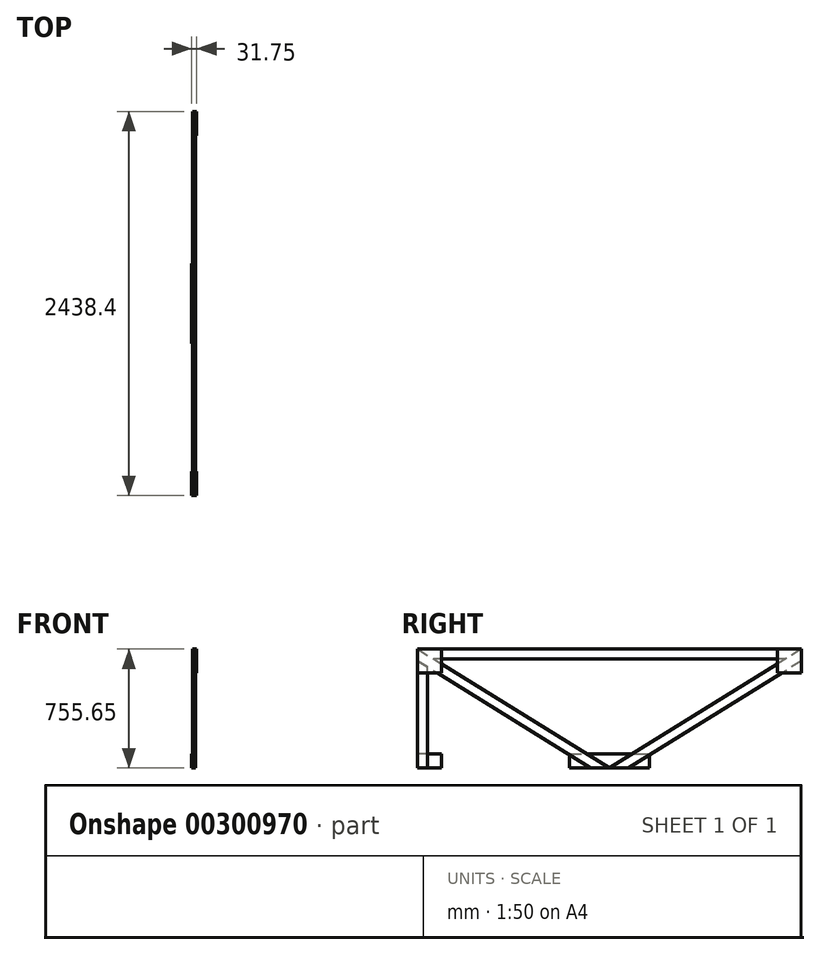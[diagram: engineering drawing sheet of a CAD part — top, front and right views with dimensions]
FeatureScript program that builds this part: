
annotation { "Feature Type Name" : "Feature", "Feature Type Description" : "" }
export const myFeature = defineFeature(function(context is Context, id is Id, definition is map)
    precondition{}
    {
        {
            var Q0;
            Q0=qCreatedBy(makeId("Right.planeOp"),FACE);
            var sketch = newSketch(context, id + "F0", { "sketchPlane" : qUnion([Q0])});
            skLineSegment(sketch, "E0.bottom", {"start": v(0, 0) * mm, "end": v(2438.4, 0) * mm, "construction": true});
            skLineSegment(sketch, "E0.left", {"start": v(0, 0) * mm, "end": v(0, 755.65) * mm, "construction": true});
            skLineSegment(sketch, "E0.right", {"start": v(2438.4, 0) * mm, "end": v(2438.4, 764.91) * mm, "construction": true});
            skLineSegment(sketch, "E1", {"start": v(0, 755.65) * mm, "end": v(1219.2, 0) * mm});
            skLineSegment(sketch, "E2.0", {"start": v(0, 680.94) * mm, "end": v(1098.66, 0) * mm});
            skLineSegment(sketch, "E3", {"start": v(0, 755.65) * mm, "end": v(0, 680.94) * mm});
            skLineSegment(sketch, "E4", {"start": v(1219.2, 0) * mm, "end": v(1098.66, 0) * mm});
            skLineSegment(sketch, "E5", {"start": v(1219.2, 0) * mm, "end": v(1219.2, 1098.2) * mm, "construction": true});
            skPoint(sketch, "E5.endSnap0", {"position": v(1219.2, 822.37) * mm});
            skLineSegment(sketch, "E6", {"start": v(1219.2, 755.65) * mm, "end": v(0, 755.65) * mm});
            skLineSegment(sketch, "E7.0", {"start": v(1221.99, 692.15) * mm, "end": v(102.45, 692.15) * mm});
            skLineSegment(sketch, "E8", {"start": v(0, 755.65) * mm, "end": v(102.45, 692.15) * mm});
            skLineSegment(sketch, "E9.MirrorCS", {"start": v(2438.4, 755.65) * mm, "end": v(2438.4, 680.94) * mm});
            skLineSegment(sketch, "E10.MirrorCS", {"start": v(2438.4, 680.94) * mm, "end": v(1339.74, 0) * mm});
            skLineSegment(sketch, "E11.MirrorCS", {"start": v(2438.4, 755.65) * mm, "end": v(1219.2, 0) * mm});
            skLineSegment(sketch, "E12.MirrorCS", {"start": v(2438.4, 755.65) * mm, "end": v(2335.95, 692.15) * mm});
            skLineSegment(sketch, "E13.MirrorCS", {"start": v(1219.2, 755.65) * mm, "end": v(2438.4, 755.65) * mm});
            skLineSegment(sketch, "E14.MirrorCS", {"start": v(1216.41, 692.15) * mm, "end": v(2335.95, 692.15) * mm});
            skLineSegment(sketch, "E15.MirrorCS", {"start": v(1219.2, 0) * mm, "end": v(1339.74, 0) * mm});
            skSolve(sketch);
        }
        {
            var Q0;
            {var subQ3=sQuery(id+"F0.wireOp",EDGE,"E9.MirrorCS");Q0=makeQuery(id+"F0.imprint","IMPRINT",FACE,{"disambiguationData":[TD([[makeQuery(id+"F0.imprint","IMPRINT",EDGE,{"derivedFrom":subQ3}),-1.0]])]});}
            var Q1;
            Q1=makeQuery(id+"F0.imprint","IMPRINT",FACE,{"disambiguationData":[TD([[makeQuery(id+"F0.imprint","IMPRINT",EDGE,{"derivedFrom":sQuery(id+"F0.wireOp",EDGE,"E2.0")}),1.0]])]});
            extrude(context, id + "F1", {"entities" : qUnion([Q0, Q1]), "depth" : 19.05 * mm});
        }
        {
            var Q0;
            Q0=makeQuery(id+"F0.imprint","IMPRINT",FACE,{"disambiguationData":[TD([[makeQuery(id+"F0.imprint","IMPRINT",EDGE,{"derivedFrom":sQuery(id+"F0.wireOp",EDGE,"E6")}),1.0]])]});
            extrude(context, id + "F2", {"entities" : qUnion([Q0]), "depth" : 19.05 * mm});
        }
        {
            var Q0;
            Q0=makeQuery(id+"F1.opExtrude","CAP_FACE",FACE,{"disambiguationData":[OSD([sQuery(id+"F0.wireOp",EDGE,"E9.MirrorCS"),sQuery(id+"F0.wireOp",EDGE,"E10.MirrorCS"),sQuery(id+"F0.wireOp",EDGE,"E11.MirrorCS"),sQuery(id+"F0.wireOp",EDGE,"E12.MirrorCS"),sQuery(id+"F0.wireOp",EDGE,"E15.MirrorCS")])],"isStart":false});
            var sketch = newSketch(context, id + "F3", { "sketchPlane" : qUnion([Q0])});
            skLineSegment(sketch, "E16.bottom", {"start": v(2438.4, 755.65) * mm, "end": v(2286, 755.65) * mm});
            skLineSegment(sketch, "E16.top", {"start": v(2438.4, 603.25) * mm, "end": v(2286, 603.25) * mm});
            skLineSegment(sketch, "E16.left", {"start": v(2438.4, 755.65) * mm, "end": v(2438.4, 603.25) * mm});
            skLineSegment(sketch, "E16.right", {"start": v(2286, 755.65) * mm, "end": v(2286, 603.25) * mm});
            skLineSegment(sketch, "E17", {"start": v(1219.2, 0) * mm, "end": v(1219.2, 1007.92) * mm, "construction": true});
            skLineSegment(sketch, "E18.MirrorCS", {"start": v(152.4, 755.65) * mm, "end": v(152.4, 603.25) * mm});
            skLineSegment(sketch, "E19.MirrorCS", {"start": v(0, 755.65) * mm, "end": v(0, 603.25) * mm});
            skLineSegment(sketch, "E20.MirrorCS", {"start": v(0, 603.25) * mm, "end": v(152.4, 603.25) * mm});
            skLineSegment(sketch, "E21.MirrorCS", {"start": v(0, 755.65) * mm, "end": v(152.4, 755.65) * mm});
            skSolve(sketch);
        }
        {
            var Q0;
            Q0 = qSketchRegion(id + "F3", true);
            extrude(context, id + "F4", {"entities" : qUnion([Q0]), "depth" : 6.35 * mm});
        }
        {
            var Q0;
            Q0=makeQuery(id+"F1.opExtrude","CAP_FACE",FACE,{"disambiguationData":[OSD([sQuery(id+"F0.wireOp",EDGE,"E9.MirrorCS"),sQuery(id+"F0.wireOp",EDGE,"E10.MirrorCS"),sQuery(id+"F0.wireOp",EDGE,"E11.MirrorCS"),sQuery(id+"F0.wireOp",EDGE,"E12.MirrorCS"),sQuery(id+"F0.wireOp",EDGE,"E15.MirrorCS")])],"isStart":true});
            var sketch = newSketch(context, id + "F5", { "sketchPlane" : qUnion([Q0])});
            skLineSegment(sketch, "E22", {"start": v(-1219.2, 0) * mm, "end": v(-965.2, 0) * mm});
            skLineSegment(sketch, "E23", {"start": v(-965.2, 0) * mm, "end": v(-965.2, 88.9) * mm});
            skLineSegment(sketch, "E24", {"start": v(-965.2, 88.9) * mm, "end": v(-1219.2, 88.9) * mm});
            skLineSegment(sketch, "E25", {"start": v(-1219.2, 0) * mm, "end": v(-1219.2, 994.5) * mm, "construction": true});
            skLineSegment(sketch, "E26.MirrorCS", {"start": v(-1219.2, 0) * mm, "end": v(-1473.2, 0) * mm});
            skLineSegment(sketch, "E27.MirrorCS", {"start": v(-1473.2, 0) * mm, "end": v(-1473.2, 88.9) * mm});
            skLineSegment(sketch, "E28.MirrorCS", {"start": v(-1473.2, 88.9) * mm, "end": v(-1219.2, 88.9) * mm});
            skLineSegment(sketch, "E29", {"start": v(0, 0) * mm, "end": v(-152.4, 0) * mm});
            skLineSegment(sketch, "E30", {"start": v(-152.4, 0) * mm, "end": v(-152.4, 88.9) * mm});
            skLineSegment(sketch, "E31", {"start": v(-152.4, 88.9) * mm, "end": v(0, 88.9) * mm});
            skLineSegment(sketch, "E32", {"start": v(0, 88.9) * mm, "end": v(0, 0) * mm});
            skSolve(sketch);
        }
        {
            var Q0;
            Q0 = qSketchRegion(id + "F5", true);
            extrude(context, id + "F6", {"entities" : qUnion([Q0]), "depth" : 6.35 * mm});
        }
        {
            var Q0;
            Q0=qCreatedBy(makeId("Right.planeOp"),FACE);
            var sketch = newSketch(context, id + "F7", { "sketchPlane" : qUnion([Q0])});
            skPoint(sketch, "E33.0", {"position": v(0, 679.45) * mm});
            skLineSegment(sketch, "E34", {"start": v(0, 679.45) * mm, "end": v(0, 0) * mm});
            skLineSegment(sketch, "E35", {"start": v(0, 0) * mm, "end": v(63.5, 0) * mm});
            skLineSegment(sketch, "E36", {"start": v(63.5, 0) * mm, "end": v(63.5, 641.59) * mm});
            skLineSegment(sketch, "E37", {"start": v(63.5, 641.59) * mm, "end": v(0, 679.45) * mm});
            skSolve(sketch);
        }
        {
            var Q0;
            Q0 = qSketchRegion(id + "F7", true);
            extrude(context, id + "F8", {"entities" : qUnion([Q0]), "depth" : 19.05 * mm});
        }
    });
